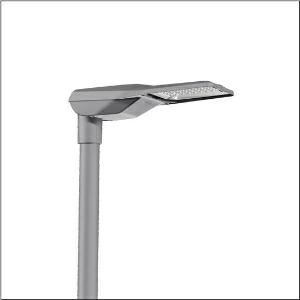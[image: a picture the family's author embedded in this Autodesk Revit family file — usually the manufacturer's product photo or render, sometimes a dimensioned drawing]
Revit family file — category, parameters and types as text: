
# Revit family: streetlight_sl_21_iq_mini___st1_0a_5xe2d41g08jb_4fff
name_source: partatom
category: Lighting Fixtures
units: mm (PartAtom-declared; Revit-internal decimal feet)

## family parameters
Cut with Voids When Loaded = No
Host = Face
Light Source = No
Part Type = Normal
Room Calculation Point = No
Round Connector Dimension = Use Diameter
Shared = No

## types (1)
- --- (1 x LED, 11290 lm, 71.6 W, 4000K)
    Apparent Load = 72 VA
    CIE Flux Codes = 40 73 97 100 100
    Color Rendering = 70
    Color Temperature = 4000K
    Default Elevation = 1800 mm
    Description = Streetlight SL 21 iQ mini, mast luminaire, primary light control with lens, of PMMA, primary optical cover: cover, of toughened safety glass, transparent, light distribution: ST1.0a, light emission: direct distribution, primary light characteristic: asymmetric, installation type: post-top, side-entry, LED, High Power LED, rated luminous flux: 11.290lm, luminous efficacy: 158lm/W, light colour: 740, colour temperature: 4000K, control: Street-Remote, Auto-Match, Temp-Guard, Lumen-Switch, Night-Set, Smart-Wire, Light-Fading, Desk-Remote (wireless, voltage-free reading and setting of iQ features in the workshop via application-optimized NFC function/RFID function), optimised constant luminous flux control (CLO 2.0), presetting dimming linear, mains connection: 220..240V, AC, 50/60Hz, start of lifetime: 72W, end of service life: 75W, reduction: 33W, luminaire housing, of diecast aluminium, powder-coated, Siteco® metallic grey (DB 702S), corrosivity category C5 mid according to DIN EN ISO 12944, please order mast flange separately, inclination adjustable: 0°, 5°, 10°, 15°, sealing non-destructively replaceable, multi-level sealing system, length: 628mm, width: 235mm, height: 110mm, mast flange for spigot size: 42mm (side-entry): 5XC10008XM4, 60/48mm (side-entry/post-top): 5XC10108XM2, 76/60mm (side-entry/post-top): 5XC10108XM1, protection rating (complete): IP66, insulation class (complete): insulation class II (safety insulation), certification: CE, ENEC, ENEC+, VDE, impact resistance: IK09, permissible operating ambient temperature for outdoor applications: -40..+50°C, standard-compliant lighting for roads and squares, packaging unit: 1 piece

Light Distribution: ST1.0a
    Height = 110 mm
    Lamp = 1 x LED
    Lamp Light Flux = 11290 lm
    Lamp Power = 71.6 W
    Lamp count = 1
    Length = 625 mm
    Luminous efficacy = 158 lm/W
    Manufacturer = Siteco
    ModVariant = No
    Model = 5XE2D41G08JB
    Number of Poles = 1
    OnlyDefault = Yes
    Power Factor = 1
    Product Name = Streetlight SL 21 iQ mini | ST1.0a
    Product group = mast luminaire | pylon top
    ProductGroupID = 6100
    Protection Class = Protection class II
    Protection Degree = IP 66
    RLX_Detail_Level = 1
    RLX_Emergency_Light_Flux = 0 lm
    RLX_Emergency_Type = 0
    RLX_Emergency_Type_DB = No
    RlxData = <blob elided: 92045 chars, md5=08711a86>
    Socket = socket
    Standby Power = 0 W
    System Light Flux = 11290 lm
    System Power = 72 W
    Type Comments = factory setting: luminous flux: 100 % | dim-lin: 254 | 746 mA
    Type Image = l_1003519.jpg
    URL = http://relux.com
    VarID = @adj_104009
    Voltage = 0 V
    Weight = 0.00 kg
    Width = 234 mm

## geometry (parser evidence)
native form markers: Blend x4, Sweep x12
no freeform markers — native parametric forms only
